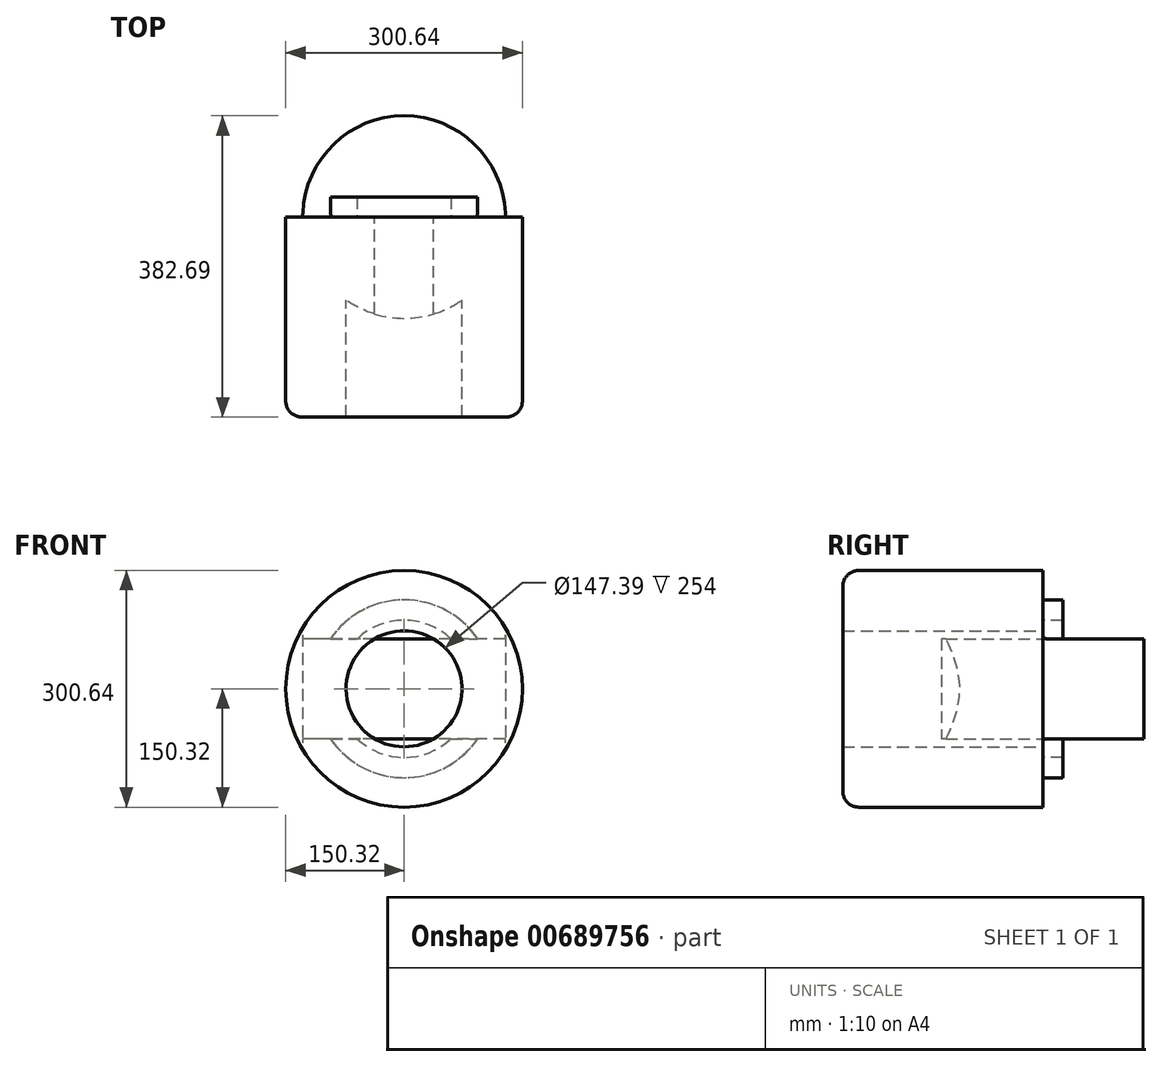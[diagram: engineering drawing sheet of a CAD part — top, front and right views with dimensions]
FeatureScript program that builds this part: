
annotation { "Feature Type Name" : "Feature", "Feature Type Description" : "" }
export const myFeature = defineFeature(function(context is Context, id is Id, definition is map)
    precondition{}
    {
        {
            var Q0;
            Q0=qCreatedBy(makeId("Front.planeOp"),FACE);
            var sketch = newSketch(context, id + "F0", { "sketchPlane" : qUnion([Q0])});
            skCircle(sketch, "E0", {"center": v(0, 0) * mm, "radius": 150.32 * mm});
            skCircle(sketch, "E1", {"center": v(0, 0) * mm, "radius": 73.7 * mm});
            skSolve(sketch);
        }
        {
            var Q0;
            Q0 = qSketchRegion(id + "F0", true);
            extrude(context, id + "F1", {"entities" : qUnion([Q0]), "depth" : 254 * mm, "offsetDistance" : 25.4 * mm});
        }
        {
            var Q0;
            Q0=makeQuery(id+"F1.opExtrude","CAP_EDGE",EDGE,{"disambiguationData":[OSD([sQuery(id+"F0.wireOp",EDGE,"E0")])],"isStart":false});
            fillet(context, id + "F2", {"entities" : qUnion([Q0]), "radius" : 20.32 * mm, "tangentPropagation" : true, "allowEdgeOverflow" : false});
        }
        {
            var Q0;
            Q0=makeQuery(id+"F1.opExtrude","CAP_FACE",FACE,{"disambiguationData":[OSD([sQuery(id+"F0.wireOp",EDGE,"E0"),sQuery(id+"F0.wireOp",EDGE,"E1")])],"isStart":true});
            var sketch = newSketch(context, id + "F3", { "sketchPlane" : qUnion([Q0])});
            skCircle(sketch, "E2", {"center": v(0, 0) * mm, "radius": 87.08 * mm});
            skCircle(sketch, "E3", {"center": v(0, 0) * mm, "radius": 112.93 * mm});
            skSolve(sketch);
        }
        {
            var Q0;
            Q0 = qSketchRegion(id + "F3", true);
            extrude(context, id + "F4", {"entities" : qUnion([Q0]), "operationType" : NewBodyOperationType.ADD, "depth" : 25.4 * mm, "offsetDistance" : 25.4 * mm});
        }
        {
            var Q0;
            Q0=qCreatedBy(makeId("Top.planeOp"),FACE);
            var sketch = newSketch(context, id + "F5", { "sketchPlane" : qUnion([Q0])});
            skCircle(sketch, "E4", {"center": v(0, 0) * mm, "radius": 128.7 * mm});
            skSolve(sketch);
        }
        {
            var Q0;
            Q0=makeQuery(id+"F5.imprint","IMPRINT",FACE,{"disambiguationData":[TD([[makeQuery(id+"F5.imprint","IMPRINT",EDGE,{"derivedFrom":sQuery(id+"F5.wireOp",EDGE,"E4")}),1.0]])]});
            extrude(context, id + "F6", {"entities" : qUnion([Q0]), "operationType" : NewBodyOperationType.ADD, "endBound" : BoundingType.SYMMETRIC, "depth" : 127 * mm, "offsetDistance" : 25.4 * mm});
        }
        {
            var Q0;
            {var subQ0=sQuery(id+"F0.wireOp",EDGE,"E0");Q0=makeQuery(id+"F6.boolean.opBoolean","INTERSECT",EDGE,{"disambiguationData":[OD(0.0)],"derivedFrom":[makeQuery(id+"F4.boolean.opBoolean","SPLIT",FACE,{"disambiguationData":[TD([makeQuery(id+"F1.opExtrude","SWEPT_FACE",FACE,{"disambiguationData":[OSD([subQ0])]})])],"derivedFrom":makeQuery(id+"F1.opExtrude","CAP_FACE",FACE,{"disambiguationData":[OSD([subQ0,sQuery(id+"F0.wireOp",EDGE,"E1")])],"isStart":true})}),makeQuery(id+"F6.opExtrude","CAP_FACE",FACE,{"disambiguationData":[OSD([sQuery(id+"F5.wireOp",EDGE,"E4")])],"isStart":true})]});}
            var Q1;
            {var subQ0=sQuery(id+"F0.wireOp",EDGE,"E0");Q1=makeQuery(id+"F6.boolean.opBoolean","INTERSECT",EDGE,{"disambiguationData":[OD(0.0)],"derivedFrom":[makeQuery(id+"F4.boolean.opBoolean","SPLIT",FACE,{"disambiguationData":[TD([makeQuery(id+"F1.opExtrude","SWEPT_FACE",FACE,{"disambiguationData":[OSD([subQ0])]})])],"derivedFrom":makeQuery(id+"F1.opExtrude","CAP_FACE",FACE,{"disambiguationData":[OSD([subQ0,sQuery(id+"F0.wireOp",EDGE,"E1")])],"isStart":true})}),makeQuery(id+"F6.opExtrude","CAP_FACE",FACE,{"disambiguationData":[OSD([sQuery(id+"F5.wireOp",EDGE,"E4")])],"isStart":false})]});}
            var Q2;
            {var subQ0=sQuery(id+"F0.wireOp",EDGE,"E0");Q2=makeQuery(id+"F6.boolean.opBoolean","INTERSECT",EDGE,{"disambiguationData":[OD(1.0)],"derivedFrom":[makeQuery(id+"F4.boolean.opBoolean","SPLIT",FACE,{"disambiguationData":[TD([makeQuery(id+"F1.opExtrude","SWEPT_FACE",FACE,{"disambiguationData":[OSD([subQ0])]})])],"derivedFrom":makeQuery(id+"F1.opExtrude","CAP_FACE",FACE,{"disambiguationData":[OSD([subQ0,sQuery(id+"F0.wireOp",EDGE,"E1")])],"isStart":true})}),makeQuery(id+"F6.opExtrude","CAP_FACE",FACE,{"disambiguationData":[OSD([sQuery(id+"F5.wireOp",EDGE,"E4")])],"isStart":false})]});}
            var Q3;
            {var subQ0=sQuery(id+"F0.wireOp",EDGE,"E0");Q3=makeQuery(id+"F6.boolean.opBoolean","INTERSECT",EDGE,{"disambiguationData":[OD(1.0)],"derivedFrom":[makeQuery(id+"F4.boolean.opBoolean","SPLIT",FACE,{"disambiguationData":[TD([makeQuery(id+"F1.opExtrude","SWEPT_FACE",FACE,{"disambiguationData":[OSD([subQ0])]})])],"derivedFrom":makeQuery(id+"F1.opExtrude","CAP_FACE",FACE,{"disambiguationData":[OSD([subQ0,sQuery(id+"F0.wireOp",EDGE,"E1")])],"isStart":true})}),makeQuery(id+"F6.opExtrude","CAP_FACE",FACE,{"disambiguationData":[OSD([sQuery(id+"F5.wireOp",EDGE,"E4")])],"isStart":true})]});}
            fillet(context, id + "F7", {"entities" : qUnion([Q0, Q1, Q2, Q3]), "radius" : 5.08 * mm, "tangentPropagation" : true, "allowEdgeOverflow" : false});
        }
    });
